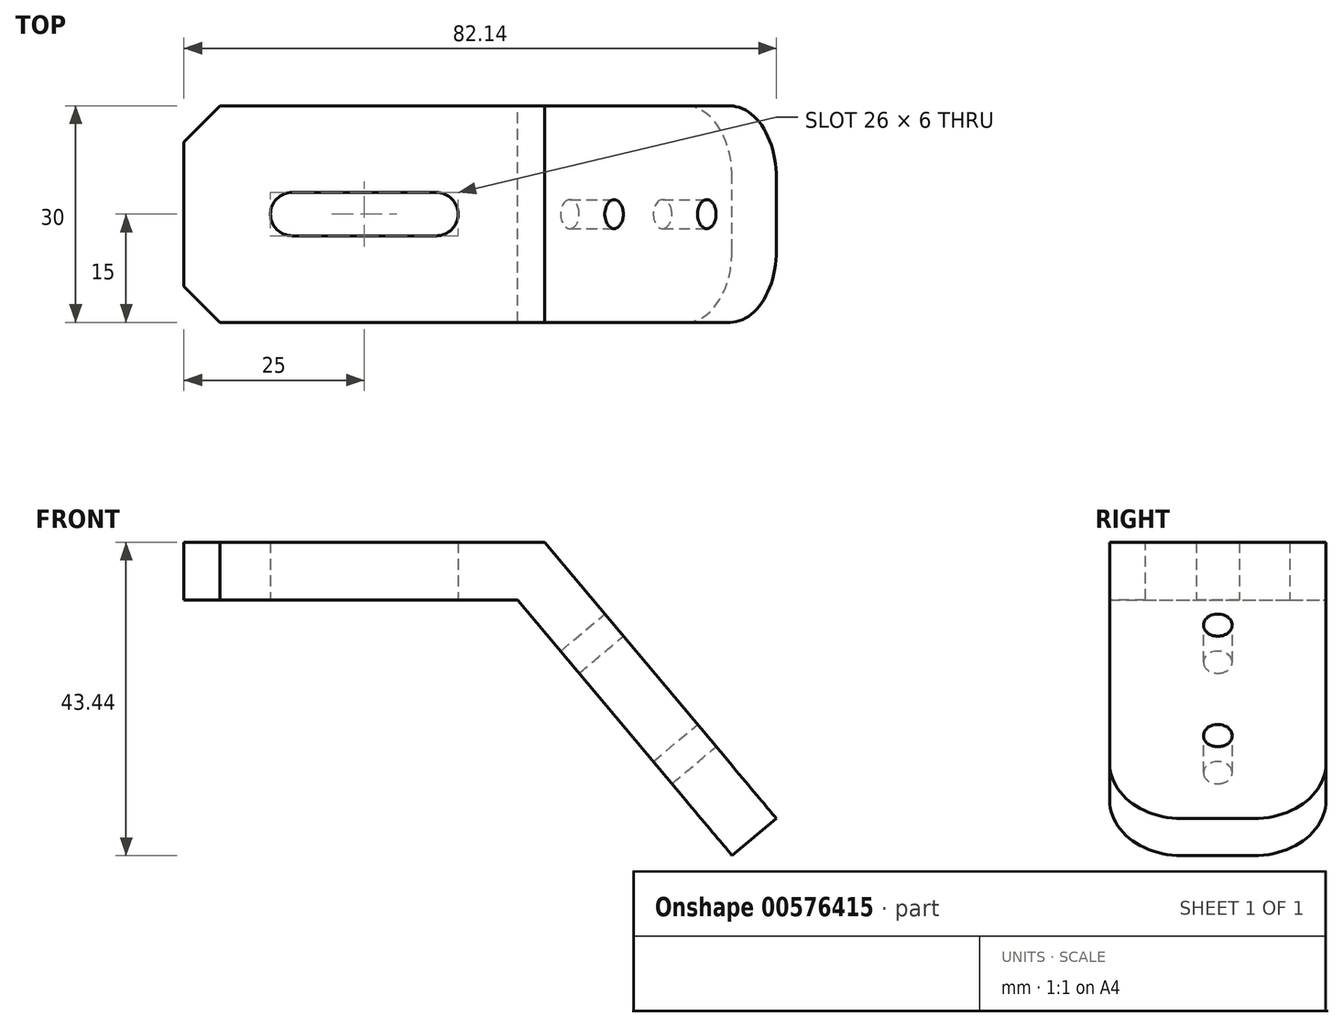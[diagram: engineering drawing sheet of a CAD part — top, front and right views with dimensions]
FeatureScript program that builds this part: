
annotation { "Feature Type Name" : "Feature", "Feature Type Description" : "" }
export const myFeature = defineFeature(function(context is Context, id is Id, definition is map)
    precondition{}
    {
        {
            var Q0;
            Q0=qCreatedBy(makeId("Front.planeOp"),FACE);
            var sketch = newSketch(context, id + "F0", { "sketchPlane" : qUnion([Q0])});
            skLineSegment(sketch, "E0", {"start": v(0, 0) * mm, "end": v(46.27, 0) * mm});
            skLineSegment(sketch, "E1", {"start": v(46.27, 0) * mm, "end": v(76.01, -35.44) * mm});
            skLineSegment(sketch, "E2.0", {"start": v(50, 8) * mm, "end": v(82.14, -30.3) * mm});
            skLineSegment(sketch, "E2.1", {"start": v(0, 8) * mm, "end": v(50, 8) * mm});
            skLineSegment(sketch, "E3", {"start": v(0, 0) * mm, "end": v(0, 8) * mm});
            skLineSegment(sketch, "E4", {"start": v(82.14, -30.3) * mm, "end": v(76.01, -35.44) * mm});
            skSolve(sketch);
        }
        {
            var Q0;
            Q0 = qSketchRegion(id + "F0", true);
            extrude(context, id + "F1", {"entities" : qUnion([Q0]), "endBound" : BoundingType.SYMMETRIC, "depth" : 30 * mm, "offsetDistance" : 25 * mm});
        }
        {
            var Q0;
            Q0=qCreatedBy(makeId("Top.planeOp"),FACE);
            var sketch = newSketch(context, id + "F2", { "sketchPlane" : qUnion([Q0])});
            skLineSegment(sketch, "E5", {"start": v(35, 0) * mm, "end": v(15, 0) * mm});
            skArc(sketch, "E6.0.startCap", {"start": v(35, 3) * mm, "mid": v(38, 0) * mm, "end": v(35, -3) * mm});
            skArc(sketch, "E6.0.endCap", {"start": v(15, -3) * mm, "mid": v(12, 0) * mm, "end": v(15, 3) * mm});
            skLineSegment(sketch, "E6.0.left", {"start": v(35, -3) * mm, "end": v(15, -3) * mm});
            skLineSegment(sketch, "E6.0.right", {"start": v(35, 3) * mm, "end": v(15, 3) * mm});
            skSolve(sketch);
        }
        {
            var Q0;
            Q0 = qSketchRegion(id + "F2", true);
            extrude(context, id + "F3", {"entities" : qUnion([Q0]), "operationType" : NewBodyOperationType.REMOVE, "endBound" : BoundingType.THROUGH_ALL, "depth" : 30 * mm, "offsetDistance" : 25 * mm});
        }
        {
            var Q0;
            Q0=makeQuery(id+"F1.opExtrude","SWEPT_FACE",FACE,{"disambiguationData":[OSD([sQuery(id+"F0.wireOp",EDGE,"E2.0")])]});
            var sketch = newSketch(context, id + "F4", { "sketchPlane" : qUnion([Q0])});
            skPoint(sketch, "E7", {"position": v(0, -41.01) * mm});
            skPoint(sketch, "E8", {"position": v(0, -61.01) * mm});
            skSolve(sketch);
        }
        {
            var Q0;
            Q0=sQuery(id+"F4.wireOp",VERTEX,"E7");
            var Q1;
            Q1=sQuery(id+"F4.wireOp",VERTEX,"E8");
            var Q2;
            Q2=makeQuery(id+"F1.opExtrude","SWEPT_BODY",BODY,{"disambiguationData":[OSD([sQuery(id+"F0.wireOp",EDGE,"E0"),sQuery(id+"F0.wireOp",EDGE,"E1"),sQuery(id+"F0.wireOp",EDGE,"E2.0"),sQuery(id+"F0.wireOp",EDGE,"E2.1"),sQuery(id+"F0.wireOp",EDGE,"E3"),sQuery(id+"F0.wireOp",EDGE,"E4")])]});
            hole(context, id + "F5", {"style" : HoleStyle.SIMPLE, "endStyle" : HoleEndStyle.THROUGH, "holeDiameter" : 4 * mm, "isTappedThrough" : true, "tappedDepth" : 12 * mm, "tapClearance" : 3, "locations" : qUnion([Q0, Q1]), "scope" : qUnion([Q2])});
        }
        {
            var Q0;
            Q0=makeQuery(id+"F1.opExtrude","CAP_EDGE",EDGE,{"disambiguationData":[OSD([sQuery(id+"F0.wireOp",EDGE,"E4")])],"isStart":false});
            var Q1;
            Q1=makeQuery(id+"F1.opExtrude","CAP_EDGE",EDGE,{"disambiguationData":[OSD([sQuery(id+"F0.wireOp",EDGE,"E4")])],"isStart":true});
            fillet(context, id + "F6", {"entities" : qUnion([Q0, Q1]), "radius" : 10 * mm, "tangentPropagation" : true, "allowEdgeOverflow" : false});
        }
        {
            var Q0;
            Q0=makeQuery(id+"F1.opExtrude","CAP_EDGE",EDGE,{"disambiguationData":[OSD([sQuery(id+"F0.wireOp",EDGE,"E3")])],"isStart":true});
            var Q1;
            Q1=makeQuery(id+"F1.opExtrude","CAP_EDGE",EDGE,{"disambiguationData":[OSD([sQuery(id+"F0.wireOp",EDGE,"E3")])],"isStart":false});
            chamfer(context, id + "F7", {"entities" : qUnion([Q0, Q1]), "width" : 5 * mm, "tangentPropagation" : true});
        }
    });
